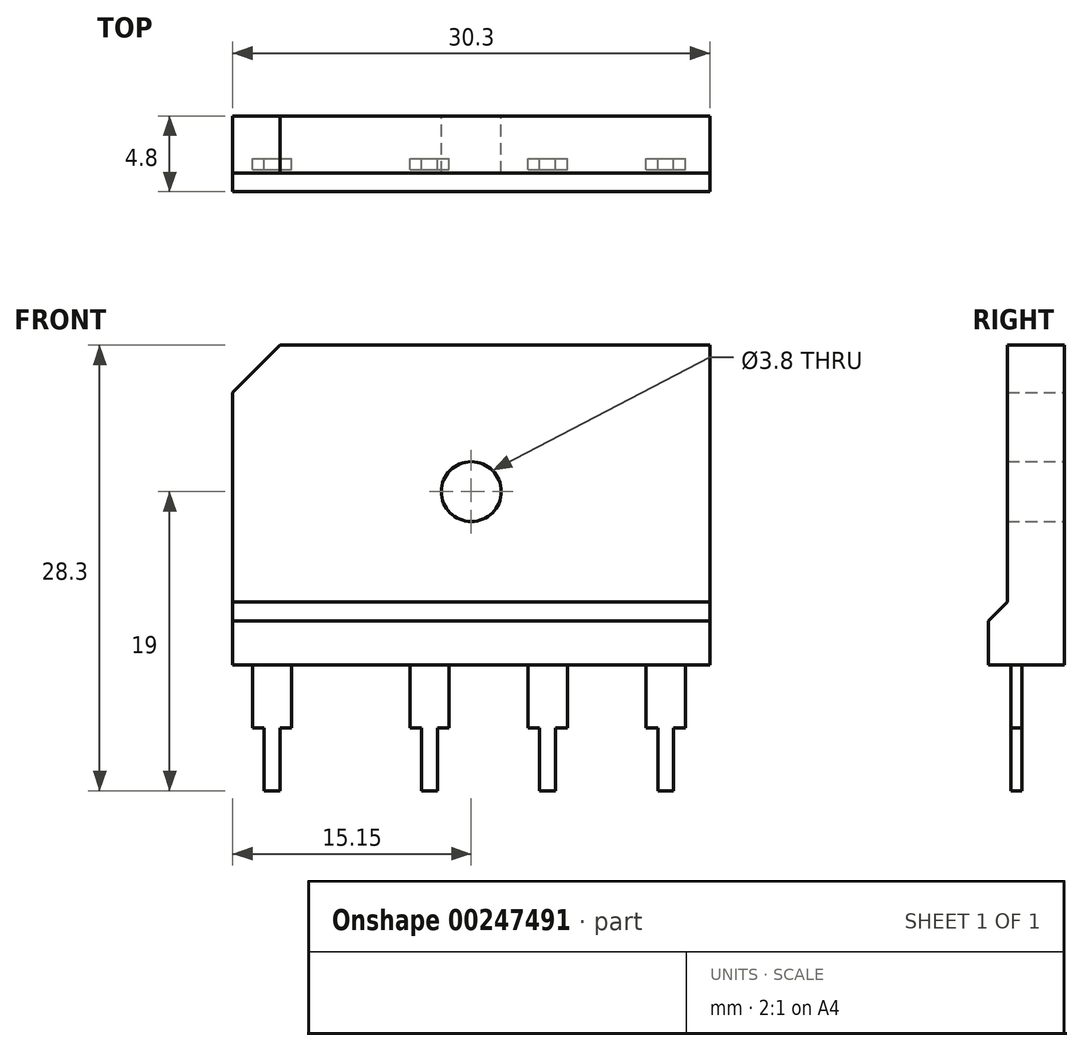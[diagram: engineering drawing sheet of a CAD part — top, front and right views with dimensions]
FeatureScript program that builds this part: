
annotation { "Feature Type Name" : "Feature", "Feature Type Description" : "" }
export const myFeature = defineFeature(function(context is Context, id is Id, definition is map)
    precondition{}
    {
        {
            var Q0;
            Q0=qCreatedBy(makeId("Front.planeOp"),FACE);
            var sketch = newSketch(context, id + "F0", { "sketchPlane" : qUnion([Q0])});
            skLineSegment(sketch, "E0.rect.bottom", {"start": v(15.15, -10.15) * mm, "end": v(-15.15, -10.15) * mm});
            skLineSegment(sketch, "E0.rect.top", {"start": v(15.15, 10.15) * mm, "end": v(-15.15, 10.15) * mm});
            skLineSegment(sketch, "E0.rect.left", {"start": v(15.15, -10.15) * mm, "end": v(15.15, 10.15) * mm});
            skLineSegment(sketch, "E0.rect.right", {"start": v(-15.15, -10.15) * mm, "end": v(-15.15, 10.15) * mm});
            skPoint(sketch, "E0.rect.middle", {"position": v(0, 0) * mm});
            skCircle(sketch, "E1", {"center": v(0, 0.85) * mm, "radius": 1.9 * mm});
            skSolve(sketch);
        }
        {
            var Q0;
            Q0=qSketchRegion(id+"F0",true);
            extrude(context, id + "F1", {"entities" : qUnion([Q0]), "depth" : 3.6 * mm});
        }
        {
            var Q0;
            Q0=makeQuery(id+"F1.opExtrude","CAP_FACE",FACE,{"disambiguationData":[OSD([sQuery(id+"F0.wireOp",EDGE,"E0.rect.bottom"),sQuery(id+"F0.wireOp",EDGE,"E0.rect.top"),sQuery(id+"F0.wireOp",EDGE,"E0.rect.left"),sQuery(id+"F0.wireOp",EDGE,"E0.rect.right"),sQuery(id+"F0.wireOp",EDGE,"E1")])],"isStart":false});
            var sketch = newSketch(context, id + "F2", { "sketchPlane" : qUnion([Q0])});
            skLineSegment(sketch, "E2.bottom", {"start": v(-15.15, -10.15) * mm, "end": v(15.15, -10.15) * mm});
            skLineSegment(sketch, "E2.top", {"start": v(-15.15, -6.15) * mm, "end": v(15.15, -6.15) * mm});
            skLineSegment(sketch, "E2.left", {"start": v(-15.15, -10.15) * mm, "end": v(-15.15, -6.15) * mm});
            skLineSegment(sketch, "E2.right", {"start": v(15.15, -10.15) * mm, "end": v(15.15, -6.15) * mm});
            skSolve(sketch);
        }
        {
            var Q0;
            Q0=qSketchRegion(id+"F2",true);
            extrude(context, id + "F3", {"entities" : qUnion([Q0]), "operationType" : NewBodyOperationType.ADD, "depth" : (4.8 - 3.6) * mm});
        }
        {
            var Q0;
            Q0=makeQuery(id+"F3.opExtrude","CAP_EDGE",EDGE,{"disambiguationData":[OSD([sQuery(id+"F2.wireOp",EDGE,"E2.top")])],"isStart":false});
            chamfer(context, id + "F4", {"entities" : qUnion([Q0]), "width" : 1.2 * mm, "tangentPropagation" : true});
        }
        {
            var Q0;
            Q0=makeQuery(id+"F1.opExtrude","SWEPT_EDGE",EDGE,{"disambiguationData":[OSD([sQuery(id+"F0.wireOp",EDGE,"E0.rect.top"),sQuery(id+"F0.wireOp",EDGE,"E0.rect.right")])]});
            chamfer(context, id + "F5", {"entities" : qUnion([Q0]), "width" : 3 * mm, "tangentPropagation" : true});
        }
        {
            var Q0;
            Q0=makeQuery(id+"F3.boolean.opBoolean","MERGE",FACE,{"derivedFrom":[makeQuery(id+"F1.opExtrude","SWEPT_FACE",FACE,{"disambiguationData":[OSD([sQuery(id+"F0.wireOp",EDGE,"E0.rect.bottom")])]}),makeQuery(id+"F3.opExtrude","SWEPT_FACE",FACE,{"disambiguationData":[OSD([sQuery(id+"F2.wireOp",EDGE,"E2.bottom")])]})]});
            var sketch = newSketch(context, id + "F6", { "sketchPlane" : qUnion([Q0])});
            skLineSegment(sketch, "E3.bottom", {"start": v(-13.9, 3.4) * mm, "end": v(-11.4, 3.4) * mm});
            skLineSegment(sketch, "E3.top", {"start": v(-13.9, 2.7) * mm, "end": v(-11.4, 2.7) * mm});
            skLineSegment(sketch, "E3.left", {"start": v(-13.9, 3.4) * mm, "end": v(-13.9, 2.7) * mm});
            skLineSegment(sketch, "E3.right", {"start": v(-11.4, 3.4) * mm, "end": v(-11.4, 2.7) * mm});
            skLineSegment(sketch, "E4.bottom", {"start": v(3.6, 3.4) * mm, "end": v(6.1, 3.4) * mm});
            skLineSegment(sketch, "E4.top", {"start": v(3.6, 2.7) * mm, "end": v(6.1, 2.7) * mm});
            skLineSegment(sketch, "E4.left", {"start": v(3.6, 3.4) * mm, "end": v(3.6, 2.7) * mm});
            skLineSegment(sketch, "E4.right", {"start": v(6.1, 3.4) * mm, "end": v(6.1, 2.7) * mm});
            skLineSegment(sketch, "E5.bottom", {"start": v(11.1, 3.4) * mm, "end": v(13.6, 3.4) * mm});
            skLineSegment(sketch, "E5.top", {"start": v(11.1, 2.7) * mm, "end": v(13.6, 2.7) * mm});
            skLineSegment(sketch, "E5.left", {"start": v(11.1, 3.4) * mm, "end": v(11.1, 2.7) * mm});
            skLineSegment(sketch, "E5.right", {"start": v(13.6, 3.4) * mm, "end": v(13.6, 2.7) * mm});
            skLineSegment(sketch, "E6", {"start": v(-12.65, 3.4) * mm, "end": v(-12.65, 2.7) * mm, "construction": true});
            skLineSegment(sketch, "E7.right", {"start": v(-1.4, 3.4) * mm, "end": v(-1.4, 2.7) * mm});
            skLineSegment(sketch, "E7.left", {"start": v(-3.9, 3.4) * mm, "end": v(-3.9, 2.7) * mm});
            skLineSegment(sketch, "E7.top", {"start": v(-3.9, 2.7) * mm, "end": v(-1.4, 2.7) * mm});
            skLineSegment(sketch, "E7.bottom", {"start": v(-3.9, 3.4) * mm, "end": v(-1.4, 3.4) * mm});
            skSolve(sketch);
        }
        {
            var Q0;
            Q0=qSketchRegion(id+"F6",true);
            extrude(context, id + "F7", {"entities" : qUnion([Q0]), "depth" : 4 * mm});
        }
        {
            var Q0;
            Q0=makeQuery(id+"F7.opExtrude","CAP_FACE",FACE,{"disambiguationData":[OSD([sQuery(id+"F6.wireOp",EDGE,"E3.bottom"),sQuery(id+"F6.wireOp",EDGE,"E3.top"),sQuery(id+"F6.wireOp",EDGE,"E3.left"),sQuery(id+"F6.wireOp",EDGE,"E3.right")])],"isStart":false});
            var sketch = newSketch(context, id + "F8", { "sketchPlane" : qUnion([Q0])});
            skLineSegment(sketch, "E8.bottom", {"start": v(-13.15, 3.4) * mm, "end": v(-12.15, 3.4) * mm});
            skLineSegment(sketch, "E8.top", {"start": v(-13.15, 2.7) * mm, "end": v(-12.15, 2.7) * mm});
            skLineSegment(sketch, "E8.left", {"start": v(-13.15, 3.4) * mm, "end": v(-13.15, 2.7) * mm});
            skLineSegment(sketch, "E8.right", {"start": v(-12.15, 3.4) * mm, "end": v(-12.15, 2.7) * mm});
            skLineSegment(sketch, "E9.bottom", {"start": v(-3.15, 3.4) * mm, "end": v(-2.15, 3.4) * mm});
            skLineSegment(sketch, "E9.top", {"start": v(-3.15, 2.7) * mm, "end": v(-2.15, 2.7) * mm});
            skLineSegment(sketch, "E9.left", {"start": v(-3.15, 3.4) * mm, "end": v(-3.15, 2.7) * mm});
            skLineSegment(sketch, "E9.right", {"start": v(-2.15, 3.4) * mm, "end": v(-2.15, 2.7) * mm});
            skLineSegment(sketch, "E10.bottom", {"start": v(4.35, 3.4) * mm, "end": v(5.35, 3.4) * mm});
            skLineSegment(sketch, "E10.top", {"start": v(4.35, 2.7) * mm, "end": v(5.35, 2.7) * mm});
            skLineSegment(sketch, "E10.left", {"start": v(4.35, 3.4) * mm, "end": v(4.35, 2.7) * mm});
            skLineSegment(sketch, "E10.right", {"start": v(5.35, 3.4) * mm, "end": v(5.35, 2.7) * mm});
            skLineSegment(sketch, "E11.bottom", {"start": v(11.85, 3.4) * mm, "end": v(12.85, 3.4) * mm});
            skLineSegment(sketch, "E11.top", {"start": v(11.85, 2.7) * mm, "end": v(12.85, 2.7) * mm});
            skLineSegment(sketch, "E11.left", {"start": v(11.85, 3.4) * mm, "end": v(11.85, 2.7) * mm});
            skLineSegment(sketch, "E11.right", {"start": v(12.85, 3.4) * mm, "end": v(12.85, 2.7) * mm});
            skSolve(sketch);
        }
        {
            var Q0;
            Q0=qSketchRegion(id+"F8",true);
            extrude(context, id + "F9", {"entities" : qUnion([Q0]), "operationType" : NewBodyOperationType.ADD, "depth" : 4 * mm});
        }
    });
